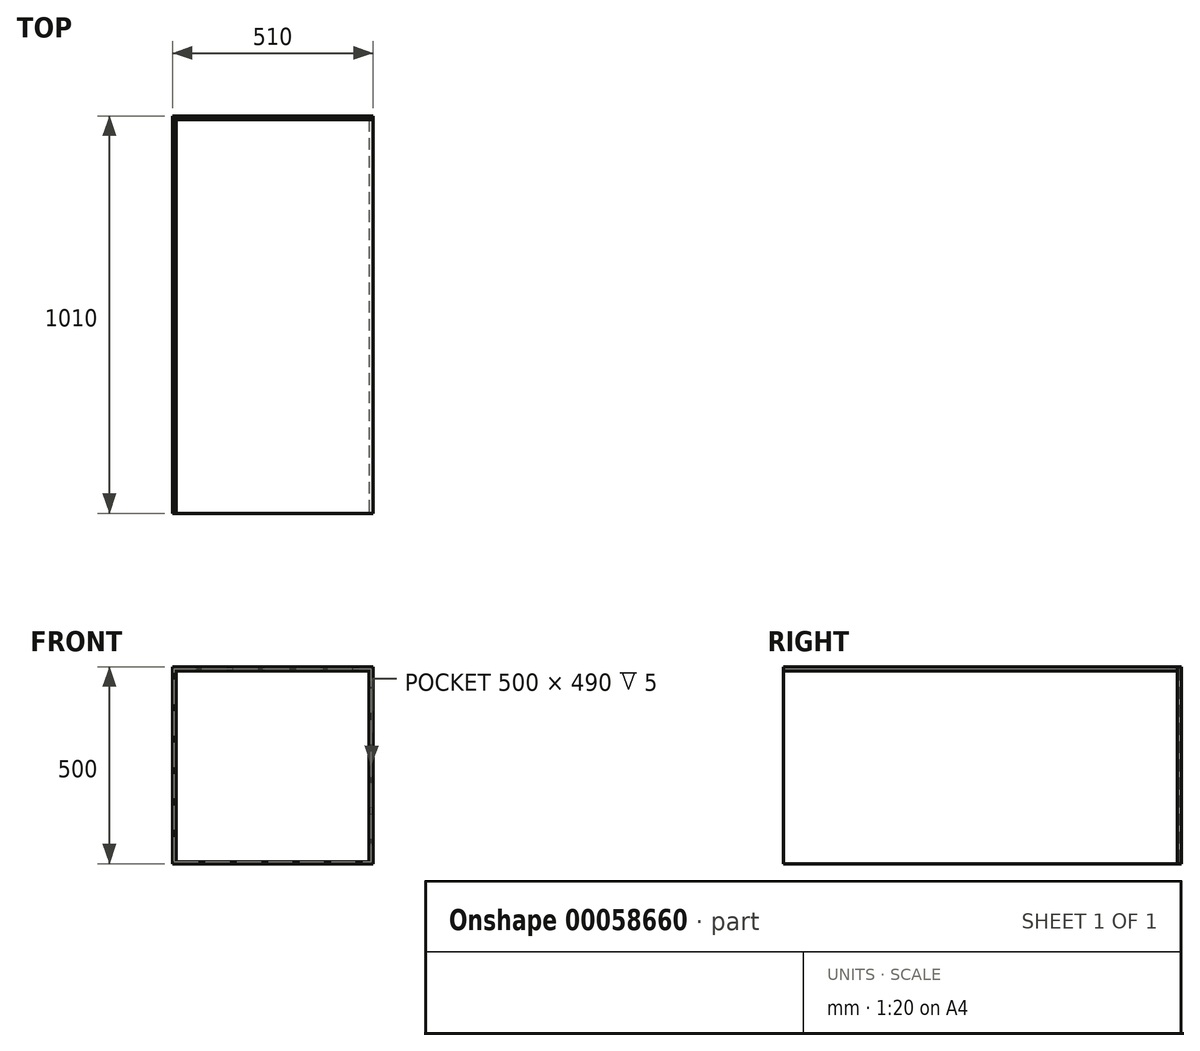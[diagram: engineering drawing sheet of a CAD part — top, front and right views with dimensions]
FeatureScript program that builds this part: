
annotation { "Feature Type Name" : "Feature", "Feature Type Description" : "" }
export const myFeature = defineFeature(function(context is Context, id is Id, definition is map)
    precondition{}
    {
        {
            var Q0;
            Q0=qCreatedBy(makeId("Front.planeOp"),FACE);
            var sketch = newSketch(context, id + "F0", { "sketchPlane" : qUnion([Q0])});
            skLineSegment(sketch, "E0.rect.bottom", {"start": v(5, 250) * mm, "end": v(-5, 250) * mm});
            skLineSegment(sketch, "E0.rect.top", {"start": v(5, -250) * mm, "end": v(-5, -250) * mm});
            skLineSegment(sketch, "E0.rect.left", {"start": v(5, 250) * mm, "end": v(5, -250) * mm});
            skLineSegment(sketch, "E0.rect.right", {"start": v(-5, 250) * mm, "end": v(-5, -250) * mm});
            skPoint(sketch, "E0.rect.middle", {"position": v(0, 0) * mm});
            skSolve(sketch);
        }
        {
            var Q0;
            Q0 = qSketchRegion(id + "F0", true);
            extrude(context, id + "F1", {"entities" : qUnion([Q0]), "depth" : 1000 * mm});
        }
        {
            var Q0;
            Q0=makeQuery(id+"F1.opExtrude","SWEPT_FACE",FACE,{"disambiguationData":[OSD([sQuery(id+"F0.wireOp",EDGE,"E0.rect.left")])]});
            var sketch = newSketch(context, id + "F2", { "sketchPlane" : qUnion([Q0])});
            skLineSegment(sketch, "E1.bottom", {"start": v(-1000, 250) * mm, "end": v(0, 250) * mm});
            skLineSegment(sketch, "E1.top", {"start": v(-1000, 240) * mm, "end": v(0, 240) * mm});
            skLineSegment(sketch, "E1.left", {"start": v(-1000, 250) * mm, "end": v(-1000, 240) * mm});
            skLineSegment(sketch, "E1.right", {"start": v(0, 250) * mm, "end": v(0, 240) * mm});
            skSolve(sketch);
        }
        {
            var Q0;
            Q0=makeQuery(id+"F2.imprint","IMPRINT",FACE,{"disambiguationData":[TD([[makeQuery(id+"F2.imprint","IMPRINT",EDGE,{"derivedFrom":sQuery(id+"F2.wireOp",EDGE,"E1.bottom")}),-1.0]])]});
            extrude(context, id + "F3", {"entities" : qUnion([Q0]), "depth" : 500 * mm});
        }
        {
            var Q0;
            Q0=makeQuery(id+"F3.opExtrude","SWEPT_FACE",FACE,{"disambiguationData":[OSD([sQuery(id+"F2.wireOp",EDGE,"E1.top")])]});
            var sketch = newSketch(context, id + "F4", { "sketchPlane" : qUnion([Q0])});
            skLineSegment(sketch, "E2.bottom", {"start": v(505, 0) * mm, "end": v(495, 0) * mm});
            skLineSegment(sketch, "E2.top", {"start": v(505, 1000) * mm, "end": v(495, 1000) * mm});
            skLineSegment(sketch, "E2.left", {"start": v(505, 0) * mm, "end": v(505, 1000) * mm});
            skLineSegment(sketch, "E2.right", {"start": v(495, 0) * mm, "end": v(495, 1000) * mm});
            skSolve(sketch);
        }
        {
            var Q0;
            Q0 = qSketchRegion(id + "F4", true);
            extrude(context, id + "F5", {"entities" : qUnion([Q0]), "depth" : 490 * mm});
        }
        {
            var Q0;
            Q0=makeQuery(id+"F3.opExtrude","SWEPT_FACE",FACE,{"disambiguationData":[OSD([sQuery(id+"F2.wireOp",EDGE,"E1.right")])]});
            var sketch = newSketch(context, id + "F6", { "sketchPlane" : qUnion([Q0])});
            skLineSegment(sketch, "E3.bottom", {"start": v(-505, 250) * mm, "end": v(5, 250) * mm});
            skLineSegment(sketch, "E3.top", {"start": v(-505, -250) * mm, "end": v(5, -250) * mm});
            skLineSegment(sketch, "E3.left", {"start": v(-505, 250) * mm, "end": v(-505, -250) * mm});
            skLineSegment(sketch, "E3.right", {"start": v(5, 250) * mm, "end": v(5, -250) * mm});
            skSolve(sketch);
        }
        {
            var Q0;
            Q0 = qSketchRegion(id + "F6", true);
            extrude(context, id + "F7", {"entities" : qUnion([Q0]), "depth" : 10 * mm});
        }
        {
            var Q0;
            Q0=makeQuery(id+"F7.opExtrude","CAP_FACE",FACE,{"disambiguationData":[OSD([sQuery(id+"F6.wireOp",EDGE,"E3.bottom"),sQuery(id+"F6.wireOp",EDGE,"E3.top"),sQuery(id+"F6.wireOp",EDGE,"E3.left"),sQuery(id+"F6.wireOp",EDGE,"E3.right")])],"isStart":true});
            shell(context, id + "F8", {"entities" : qUnion([Q0]), "thickness" : 5 * mm});
        }
    });
